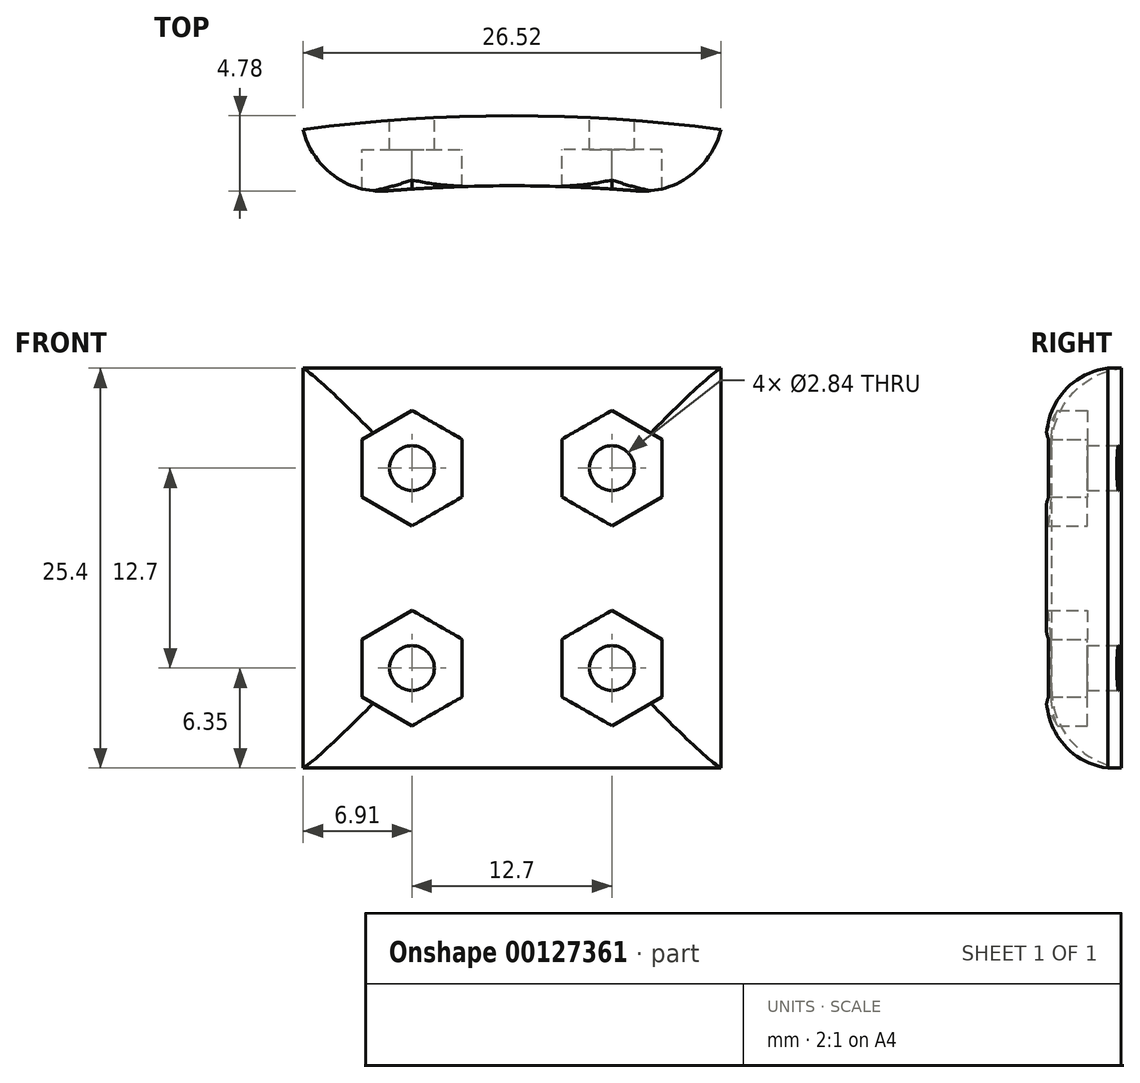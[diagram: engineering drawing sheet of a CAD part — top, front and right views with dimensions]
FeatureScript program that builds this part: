
annotation { "Feature Type Name" : "Feature", "Feature Type Description" : "" }
export const myFeature = defineFeature(function(context is Context, id is Id, definition is map)
    precondition{}
    {
        {
            var Q0;
            Q0=qCreatedBy(makeId("Top.planeOp"),FACE);
            var sketch = newSketch(context, id + "F0", { "sketchPlane" : qUnion([Q0])});
            skCircle(sketch, "E0", {"center": v(0, 0) * mm, "radius": 101.6 * mm});
            skCircle(sketch, "E1.0", {"center": v(0, 0) * mm, "radius": 97.16 * mm});
            skLineSegment(sketch, "E2", {"start": v(0, 0) * mm, "end": v(0, 101.6) * mm});
            skLineSegment(sketch, "E3", {"start": v(0, 0) * mm, "end": v(13.26, 100.73) * mm});
            skLineSegment(sketch, "E4.MirrorCS", {"start": v(0, 0) * mm, "end": v(-13.26, 100.73) * mm});
            skSolve(sketch);
        }
        {
            var Q0;
            {var subQ0=sQuery(id+"F0.wireOp",EDGE,"E2");var subQ1=sQuery(id+"F0.wireOp",EDGE,"E0");var subQ2=makeQuery(id+"F0.imprint","INTERSECT",VERTEX,{"derivedFrom":[subQ1,subQ0]});Q0=makeQuery(id+"F0.imprint","IMPRINT",FACE,{"disambiguationData":[TD([[makeQuery(id+"F0.imprint","IMPRINT",EDGE,{"disambiguationData":[TD([[subQ2,-1.0]])],"derivedFrom":subQ1}),1.0]])]});}
            var Q1;
            {var subQ0=sQuery(id+"F0.wireOp",EDGE,"E2");var subQ1=sQuery(id+"F0.wireOp",EDGE,"E0");var subQ2=makeQuery(id+"F0.imprint","INTERSECT",VERTEX,{"derivedFrom":[subQ1,subQ0]});Q1=makeQuery(id+"F0.imprint","IMPRINT",FACE,{"disambiguationData":[TD([[makeQuery(id+"F0.imprint","IMPRINT",EDGE,{"disambiguationData":[TD([[subQ2,1.0]])],"derivedFrom":subQ1}),1.0]])]});}
            extrude(context, id + "F1", {"entities" : qUnion([Q0, Q1]), "endBound" : BoundingType.SYMMETRIC, "depth" : 25.4 * mm});
        }
        {
            var Q0;
            Q0=sQuery(id+"F0.wireOp",EDGE,"E2");
            cPlane(context, id + "F2", {"entities" : qUnion([Q0]), "cplaneType" : CPlaneType.LINE_ANGLE, "offset" : 25.4 * mm, "angle" : 90 * degree, "width" : 152.4 * mm, "height" : 152.4 * mm});
        }
        {
            var Q0;
            Q0=qCreatedBy(id+"F2.planeOp",FACE);
            var sketch = newSketch(context, id + "F3", { "sketchPlane" : qUnion([Q0])});
            skLineSegment(sketch, "E5", {"start": v(101.6, 0) * mm, "end": v(101.6, 25.4) * mm});
            skSolve(sketch);
        }
        {
            var Q0;
            Q0=sQuery(id+"F3.wireOp",EDGE,"E5");
            cPlane(context, id + "F4", {"entities" : qUnion([Q0]), "cplaneType" : CPlaneType.LINE_ANGLE, "offset" : 25.4 * mm, "angle" : 90 * degree, "width" : 152.4 * mm, "height" : 152.4 * mm});
        }
        {
            var Q0;
            Q0=qCreatedBy(id+"F4.planeOp",FACE);
            var sketch = newSketch(context, id + "F5", { "sketchPlane" : qUnion([Q0])});
            skLineSegment(sketch, "E6.bottom", {"start": v(-6.35, -6.35) * mm, "end": v(6.35, -6.35) * mm});
            skLineSegment(sketch, "E6.top", {"start": v(-6.35, 6.35) * mm, "end": v(6.35, 6.35) * mm});
            skLineSegment(sketch, "E6.left", {"start": v(-6.35, -6.35) * mm, "end": v(-6.35, 6.35) * mm});
            skLineSegment(sketch, "E6.right", {"start": v(6.35, -6.35) * mm, "end": v(6.35, 6.35) * mm});
            skPoint(sketch, "E6.middle", {"position": v(0, 0) * mm});
            skCircle(sketch, "E7", {"center": v(6.35, -6.35) * mm, "radius": 1.42 * mm});
            skCircle(sketch, "E8", {"center": v(-6.35, -6.35) * mm, "radius": 1.42 * mm});
            skCircle(sketch, "E9", {"center": v(-6.35, 6.35) * mm, "radius": 1.42 * mm});
            skCircle(sketch, "E10", {"center": v(6.35, 6.35) * mm, "radius": 1.42 * mm});
            skCircle(sketch, "E11.cCircle", {"center": v(-6.35, 6.35) * mm, "radius": 3.18 * mm, "construction": true});
            skLineSegment(sketch, "E11.0", {"start": v(-6.35, 10.02) * mm, "end": v(-3.18, 8.18) * mm});
            skLineSegment(sketch, "E11.1", {"start": v(-3.18, 8.18) * mm, "end": v(-3.18, 4.52) * mm});
            skLineSegment(sketch, "E11.2", {"start": v(-3.17, 4.52) * mm, "end": v(-6.35, 2.68) * mm});
            skLineSegment(sketch, "E11.3", {"start": v(-6.35, 2.68) * mm, "end": v(-9.53, 4.52) * mm});
            skLineSegment(sketch, "E11.4", {"start": v(-9.52, 4.52) * mm, "end": v(-9.53, 8.18) * mm});
            skLineSegment(sketch, "E11.5", {"start": v(-9.53, 8.18) * mm, "end": v(-6.35, 10.02) * mm});
            skPoint(sketch, "E11.0.midPoint", {"position": v(-4.76, 9.1) * mm});
            skLineSegment(sketch, "E12", {"start": v(-6.35, 6.35) * mm, "end": v(-3.18, 6.35) * mm});
            skCircle(sketch, "E13.cCircle", {"center": v(6.35, 6.35) * mm, "radius": 3.18 * mm, "construction": true});
            skLineSegment(sketch, "E13.0", {"start": v(6.35, 10.02) * mm, "end": v(9.52, 8.18) * mm});
            skLineSegment(sketch, "E13.1", {"start": v(9.52, 8.18) * mm, "end": v(9.52, 4.52) * mm});
            skLineSegment(sketch, "E13.2", {"start": v(9.52, 4.52) * mm, "end": v(6.35, 2.68) * mm});
            skLineSegment(sketch, "E13.3", {"start": v(6.35, 2.68) * mm, "end": v(3.18, 4.52) * mm});
            skLineSegment(sketch, "E13.4", {"start": v(3.17, 4.52) * mm, "end": v(3.17, 8.18) * mm});
            skLineSegment(sketch, "E13.5", {"start": v(3.17, 8.18) * mm, "end": v(6.35, 10.02) * mm});
            skPoint(sketch, "E13.0.midPoint", {"position": v(7.94, 9.1) * mm});
            skCircle(sketch, "E14.cCircle", {"center": v(-6.35, -6.35) * mm, "radius": 3.18 * mm, "construction": true});
            skLineSegment(sketch, "E14.0", {"start": v(-6.35, -2.68) * mm, "end": v(-3.17, -4.52) * mm});
            skLineSegment(sketch, "E14.1", {"start": v(-3.18, -4.52) * mm, "end": v(-3.18, -8.18) * mm});
            skLineSegment(sketch, "E14.2", {"start": v(-3.18, -8.18) * mm, "end": v(-6.35, -10.02) * mm});
            skLineSegment(sketch, "E14.3", {"start": v(-6.35, -10.02) * mm, "end": v(-9.52, -8.18) * mm});
            skLineSegment(sketch, "E14.4", {"start": v(-9.52, -8.18) * mm, "end": v(-9.52, -4.52) * mm});
            skLineSegment(sketch, "E14.5", {"start": v(-9.52, -4.52) * mm, "end": v(-6.35, -2.68) * mm});
            skPoint(sketch, "E14.0.midPoint", {"position": v(-4.76, -3.6) * mm});
            skCircle(sketch, "E15.cCircle", {"center": v(6.35, -6.35) * mm, "radius": 3.18 * mm, "construction": true});
            skLineSegment(sketch, "E15.0", {"start": v(6.35, -2.68) * mm, "end": v(9.53, -4.52) * mm});
            skLineSegment(sketch, "E15.1", {"start": v(9.52, -4.52) * mm, "end": v(9.52, -8.18) * mm});
            skLineSegment(sketch, "E15.2", {"start": v(9.52, -8.18) * mm, "end": v(6.35, -10.02) * mm});
            skLineSegment(sketch, "E15.3", {"start": v(6.35, -10.02) * mm, "end": v(3.17, -8.18) * mm});
            skLineSegment(sketch, "E15.4", {"start": v(3.18, -8.18) * mm, "end": v(3.18, -4.52) * mm});
            skLineSegment(sketch, "E15.5", {"start": v(3.18, -4.52) * mm, "end": v(6.35, -2.68) * mm});
            skPoint(sketch, "E15.0.midPoint", {"position": v(7.94, -3.6) * mm});
            skSolve(sketch);
        }
        {
            var Q0;
            {var subQ0=sQuery(id+"F5.wireOp",EDGE,"E6.right");var subQ1=sQuery(id+"F5.wireOp",EDGE,"E6.bottom");var subQ2=makeQuery(id+"F5.imprint","INTERSECT",VERTEX,{"derivedFrom":[subQ1,subQ0]});Q0=makeQuery(id+"F5.imprint","IMPRINT",FACE,{"disambiguationData":[TD([[makeQuery(id+"F5.imprint","IMPRINT",EDGE,{"disambiguationData":[TD([[subQ2,1.0]])],"derivedFrom":subQ1}),-1.0]])]});}
            var Q1;
            {var subQ0=sQuery(id+"F5.wireOp",EDGE,"E6.right");var subQ1=sQuery(id+"F5.wireOp",EDGE,"E6.bottom");var subQ2=makeQuery(id+"F5.imprint","INTERSECT",VERTEX,{"derivedFrom":[subQ1,subQ0]});Q1=makeQuery(id+"F5.imprint","IMPRINT",FACE,{"disambiguationData":[TD([[makeQuery(id+"F5.imprint","IMPRINT",EDGE,{"disambiguationData":[TD([[subQ2,1.0]])],"derivedFrom":subQ1}),1.0]])]});}
            var Q2;
            {var subQ0=sQuery(id+"F5.wireOp",EDGE,"E6.left");var subQ1=sQuery(id+"F5.wireOp",EDGE,"E6.bottom");var subQ2=makeQuery(id+"F5.imprint","INTERSECT",VERTEX,{"derivedFrom":[subQ1,subQ0]});Q2=makeQuery(id+"F5.imprint","IMPRINT",FACE,{"disambiguationData":[TD([[makeQuery(id+"F5.imprint","IMPRINT",EDGE,{"disambiguationData":[TD([[subQ2,-1.0]])],"derivedFrom":subQ1}),-1.0]])]});}
            var Q3;
            {var subQ0=sQuery(id+"F5.wireOp",EDGE,"E6.left");var subQ1=sQuery(id+"F5.wireOp",EDGE,"E6.bottom");var subQ2=makeQuery(id+"F5.imprint","INTERSECT",VERTEX,{"derivedFrom":[subQ1,subQ0]});Q3=makeQuery(id+"F5.imprint","IMPRINT",FACE,{"disambiguationData":[TD([[makeQuery(id+"F5.imprint","IMPRINT",EDGE,{"disambiguationData":[TD([[subQ2,-1.0]])],"derivedFrom":subQ1}),1.0]])]});}
            var Q4;
            {var subQ0=sQuery(id+"F5.wireOp",EDGE,"E6.right");var subQ1=sQuery(id+"F5.wireOp",EDGE,"E6.top");var subQ2=makeQuery(id+"F5.imprint","INTERSECT",VERTEX,{"derivedFrom":[subQ1,subQ0]});Q4=makeQuery(id+"F5.imprint","IMPRINT",FACE,{"disambiguationData":[TD([[makeQuery(id+"F5.imprint","IMPRINT",EDGE,{"disambiguationData":[TD([[subQ2,1.0]])],"derivedFrom":subQ1}),1.0]])]});}
            var Q5;
            {var subQ0=sQuery(id+"F5.wireOp",EDGE,"E6.right");var subQ1=sQuery(id+"F5.wireOp",EDGE,"E6.top");var subQ2=makeQuery(id+"F5.imprint","INTERSECT",VERTEX,{"derivedFrom":[subQ1,subQ0]});Q5=makeQuery(id+"F5.imprint","IMPRINT",FACE,{"disambiguationData":[TD([[makeQuery(id+"F5.imprint","IMPRINT",EDGE,{"disambiguationData":[TD([[subQ2,1.0]])],"derivedFrom":subQ1}),-1.0]])]});}
            var Q6;
            {var subQ0=sQuery(id+"F5.wireOp",EDGE,"E6.left");var subQ1=sQuery(id+"F5.wireOp",EDGE,"E6.top");var subQ2=makeQuery(id+"F5.imprint","INTERSECT",VERTEX,{"derivedFrom":[subQ1,subQ0]});Q6=makeQuery(id+"F5.imprint","IMPRINT",FACE,{"disambiguationData":[TD([[makeQuery(id+"F5.imprint","IMPRINT",EDGE,{"disambiguationData":[TD([[subQ2,-1.0]])],"derivedFrom":subQ1}),1.0]])]});}
            var Q7;
            {var subQ0=sQuery(id+"F5.wireOp",EDGE,"E6.left");var subQ1=sQuery(id+"F5.wireOp",EDGE,"E6.top");var subQ2=makeQuery(id+"F5.imprint","INTERSECT",VERTEX,{"derivedFrom":[subQ1,subQ0]});Q7=makeQuery(id+"F5.imprint","IMPRINT",FACE,{"disambiguationData":[TD([[makeQuery(id+"F5.imprint","IMPRINT",EDGE,{"disambiguationData":[TD([[subQ2,-1.0]])],"derivedFrom":subQ1}),-1.0]])]});}
            extrude(context, id + "F6", {"entities" : qUnion([Q0, Q1, Q2, Q3, Q4, Q5, Q6, Q7]), "operationType" : NewBodyOperationType.REMOVE, "oppositeDirection" : true, "depth" : 25.4 * mm});
        }
        {
            var Q0;
            Q0=makeQuery(id+"F1.opExtrude","CAP_EDGE",EDGE,{"disambiguationData":[OSD([sQuery(id+"F0.wireOp",EDGE,"E1.0")])],"isStart":false});
            var Q1;
            Q1=makeQuery(id+"F1.opExtrude","SWEPT_EDGE",EDGE,{"disambiguationData":[OSD([sQuery(id+"F0.wireOp",EDGE,"E1.0"),sQuery(id+"F0.wireOp",EDGE,"E3")])]});
            var Q2;
            Q2=makeQuery(id+"F1.opExtrude","CAP_EDGE",EDGE,{"disambiguationData":[OSD([sQuery(id+"F0.wireOp",EDGE,"E1.0")])],"isStart":true});
            var Q3;
            Q3=makeQuery(id+"F1.opExtrude","SWEPT_EDGE",EDGE,{"disambiguationData":[OSD([sQuery(id+"F0.wireOp",EDGE,"E1.0"),sQuery(id+"F0.wireOp",EDGE,"E4.MirrorCS")])]});
            fillet(context, id + "F7", {"entities" : qUnion([Q0, Q1, Q2, Q3]), "radius" : 5.08 * mm, "tangentPropagation" : true, "allowEdgeOverflow" : false});
        }
        {
            var Q0;
            Q0=makeQuery(id+"F5.imprint","IMPRINT",FACE,{"disambiguationData":[TD([[makeQuery(id+"F5.imprint","IMPRINT",EDGE,{"derivedFrom":sQuery(id+"F5.wireOp",EDGE,"E13.0")}),-1.0]])]});
            var Q1;
            {var subQ0=sQuery(id+"F5.wireOp",EDGE,"E13.3");Q1=makeQuery(id+"F5.imprint","IMPRINT",FACE,{"disambiguationData":[TD([[makeQuery(id+"F5.imprint","IMPRINT",EDGE,{"derivedFrom":subQ0}),-1.0]])]});}
            var Q2;
            {var subQ0=sQuery(id+"F5.wireOp",EDGE,"E15.0");Q2=makeQuery(id+"F5.imprint","IMPRINT",FACE,{"disambiguationData":[TD([[makeQuery(id+"F5.imprint","IMPRINT",EDGE,{"derivedFrom":subQ0}),-1.0]])]});}
            var Q3;
            {var subQ0=sQuery(id+"F5.wireOp",EDGE,"E15.5");Q3=makeQuery(id+"F5.imprint","IMPRINT",FACE,{"disambiguationData":[TD([[makeQuery(id+"F5.imprint","IMPRINT",EDGE,{"derivedFrom":subQ0}),-1.0]])]});}
            var Q4;
            {var subQ0=sQuery(id+"F5.wireOp",EDGE,"E14.2");Q4=makeQuery(id+"F5.imprint","IMPRINT",FACE,{"disambiguationData":[TD([[makeQuery(id+"F5.imprint","IMPRINT",EDGE,{"derivedFrom":subQ0}),-1.0]])]});}
            var Q5;
            {var subQ0=sQuery(id+"F5.wireOp",EDGE,"E14.0");Q5=makeQuery(id+"F5.imprint","IMPRINT",FACE,{"disambiguationData":[TD([[makeQuery(id+"F5.imprint","IMPRINT",EDGE,{"derivedFrom":subQ0}),-1.0]])]});}
            var Q6;
            {var subQ0=sQuery(id+"F5.wireOp",EDGE,"E11.2");Q6=makeQuery(id+"F5.imprint","IMPRINT",FACE,{"disambiguationData":[TD([[makeQuery(id+"F5.imprint","IMPRINT",EDGE,{"derivedFrom":subQ0}),-1.0]])]});}
            var Q7;
            {var subQ3=sQuery(id+"F5.wireOp",EDGE,"E11.0");Q7=makeQuery(id+"F5.imprint","IMPRINT",FACE,{"disambiguationData":[TD([[makeQuery(id+"F5.imprint","IMPRINT",EDGE,{"derivedFrom":subQ3}),-1.0]])]});}
            extrude(context, id + "F8", {"entities" : qUnion([Q0, Q1, Q2, Q3, Q4, Q5, Q6, Q7]), "operationType" : NewBodyOperationType.REMOVE, "oppositeDirection" : true, "depth" : 25.4 * mm, "hasSecondDirection" : true, "secondDirectionOppositeDirection" : true, "secondDirectionDepth" : 2.16 * mm});
        }
        {
            var Q0;
            {var subQ0=sQuery(id+"F5.wireOp",EDGE,"E12");var subQ1=sQuery(id+"F5.wireOp",EDGE,"E6.left");var subQ2=makeQuery(id+"F5.imprint","INTERSECT",VERTEX,{"derivedFrom":[subQ1,subQ0]});Q0=makeQuery(id+"F5.imprint","IMPRINT",FACE,{"disambiguationData":[TD([[makeQuery(id+"F5.imprint","IMPRINT",EDGE,{"disambiguationData":[TD([[subQ2,1.0]])],"derivedFrom":subQ1}),1.0]])]});}
            var Q1;
            {var subQ0=sQuery(id+"F5.wireOp",EDGE,"E12");var subQ1=sQuery(id+"F5.wireOp",EDGE,"E6.left");var subQ2=makeQuery(id+"F5.imprint","INTERSECT",VERTEX,{"derivedFrom":[subQ1,subQ0]});Q1=makeQuery(id+"F5.imprint","IMPRINT",FACE,{"disambiguationData":[TD([[makeQuery(id+"F5.imprint","IMPRINT",EDGE,{"disambiguationData":[TD([[subQ2,1.0]])],"derivedFrom":subQ1}),-1.0]])]});}
            extrude(context, id + "F9", {"entities" : qUnion([Q0, Q1]), "operationType" : NewBodyOperationType.REMOVE, "oppositeDirection" : true, "depth" : 25.4 * mm});
        }
    });
